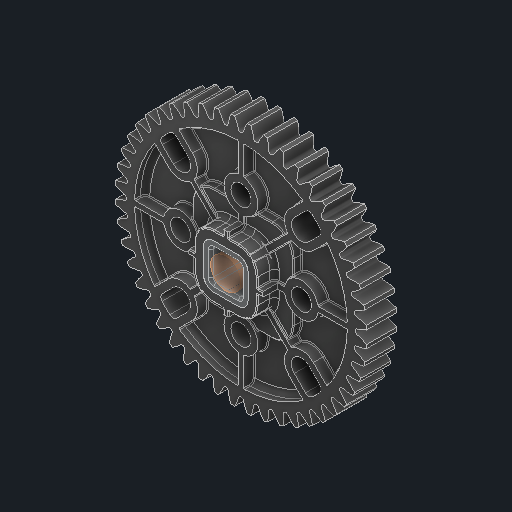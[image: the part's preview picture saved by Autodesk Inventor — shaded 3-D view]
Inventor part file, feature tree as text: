
AUTODESK INVENTOR PART (.ipt)
format: ipt  version: 2025 (Build 290162000, 162)  size: 2,923,008 bytes
history: native  units: in
note: dims shown in document units (in); Inventor stores cm internally (conversion verified against a paired STEP export)
features: other x3, extrude x3, sketch x2
ambient origin geometry x8: Origin, YZ Plane, XZ Plane, XY Plane, X Axis, Y Axis, Z Axis, Center Point
bodies: Solid1 (feature_tree), Solid2 (feature_tree)
feature tree (8):
  other  "276-7573-001_OVERMOLD Rev7_48T 24DP Gear_1:1"
  extrude  "Extrusion1"  Depth=0.3937in TaperAngle=0.0deg
  extrude  "Extrusion2"  Depth=0.125in TaperAngle=0.0deg
  other  "Srf1"
  sketch  "Sketch2"  dims[d0=0.25in d1=0.3937in d2=0.0in]
  sketch  "Sketch3"  dims[d3=0.125in d4=0.0in d5=0.125in d6=0.0in]
  other  "276-7573-002 Rev7_2:1"
  extrude  "ExtrusionSrf1"  [1 undecoded]
note: 1 required parameter value undecoded (feature->parameter linkage not recoverable at this tier; creation-order binding heuristic only, values carry confidence <= 0.55)
